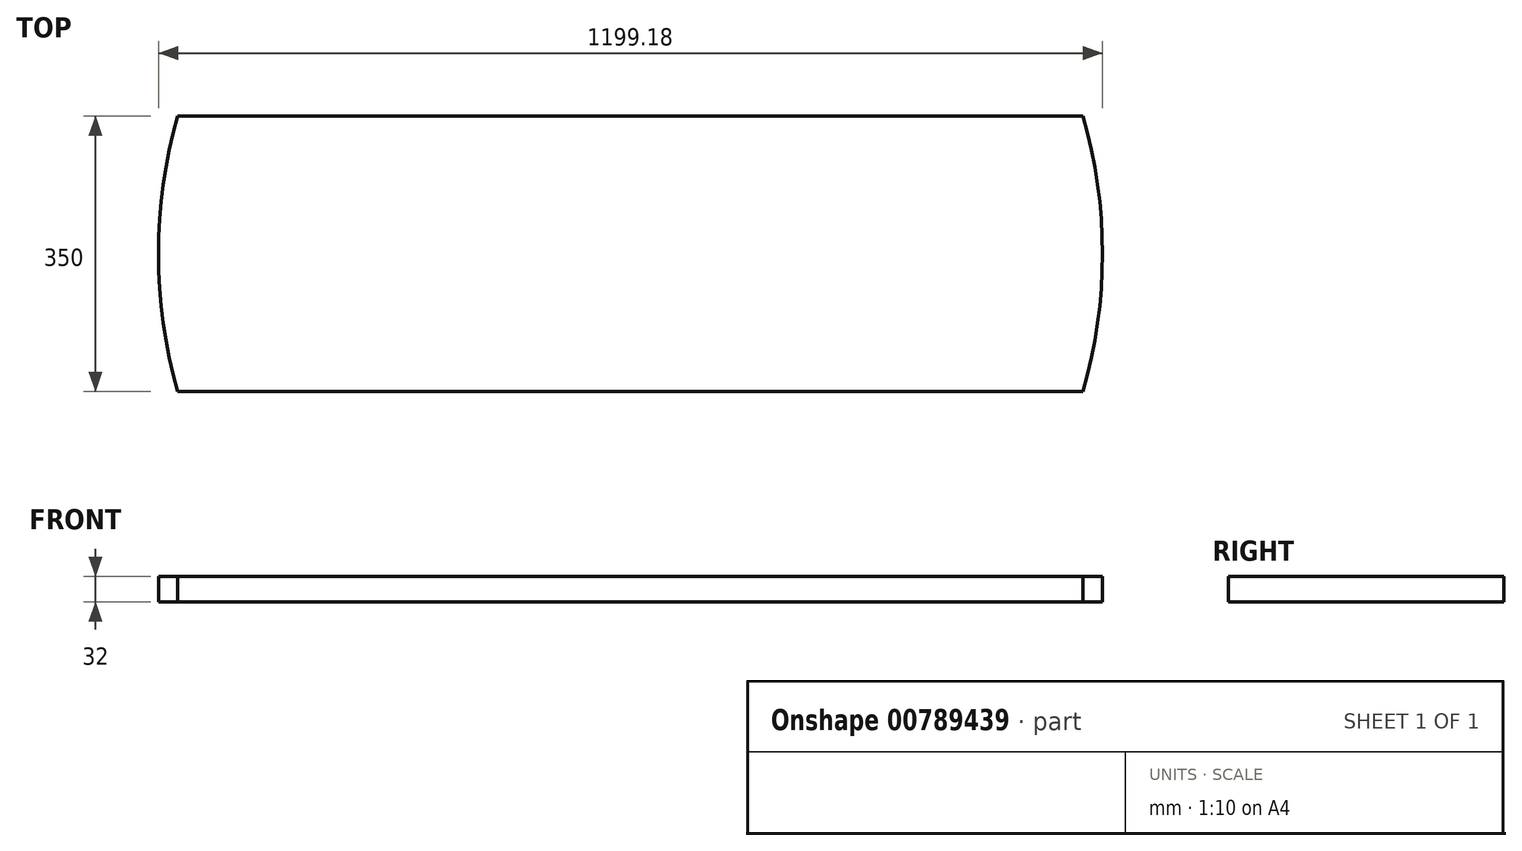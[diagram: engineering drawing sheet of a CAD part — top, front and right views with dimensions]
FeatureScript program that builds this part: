
annotation { "Feature Type Name" : "Feature", "Feature Type Description" : "" }
export const myFeature = defineFeature(function(context is Context, id is Id, definition is map)
    precondition{}
    {
        {
            var Q0;
            Q0=qCreatedBy(makeId("Top.planeOp"),FACE);
            var sketch = newSketch(context, id + "F0", { "sketchPlane" : qUnion([Q0])});
            skLineSegment(sketch, "E0.bottom", {"start": v(-596.28, -141.14) * mm, "end": v(553.72, -141.14) * mm});
            skLineSegment(sketch, "E0.top", {"start": v(-596.28, 208.86) * mm, "end": v(553.72, 208.86) * mm});
            skArc(sketch, "E1", {"start": v(-596.28, 208.86) * mm, "mid": v(-620.87, 33.86) * mm, "end": v(-596.28, -141.14) * mm});
            skLineSegment(sketch, "E2", {"start": v(-21.28, -141.14) * mm, "end": v(-21.28, -272.35) * mm});
            skArc(sketch, "E3.MirrorCS", {"start": v(553.72, 208.86) * mm, "mid": v(578.3, 33.86) * mm, "end": v(553.72, -141.14) * mm});
            skPoint(sketch, "E0.left.end.orphan", {"position": v(-621.28, 208.86) * mm});
            skPoint(sketch, "E4.orphan", {"position": v(-621.28, -141.14) * mm});
            skPoint(sketch, "E5.orphan", {"position": v(578.72, -141.14) * mm});
            skSolve(sketch);
        }
        {
            var Q0;
            Q0=makeQuery(id+"F0.imprint","IMPRINT",FACE,{"disambiguationData":[TD([[makeQuery(id+"F0.imprint","IMPRINT",EDGE,{"derivedFrom":sQuery(id+"F0.wireOp",EDGE,"E0.bottom")}),1.0]])]});
            extrude(context, id + "F1", {"entities" : qUnion([Q0]), "depth" : 32 * mm, "offsetDistance" : 25 * mm});
        }
    });
